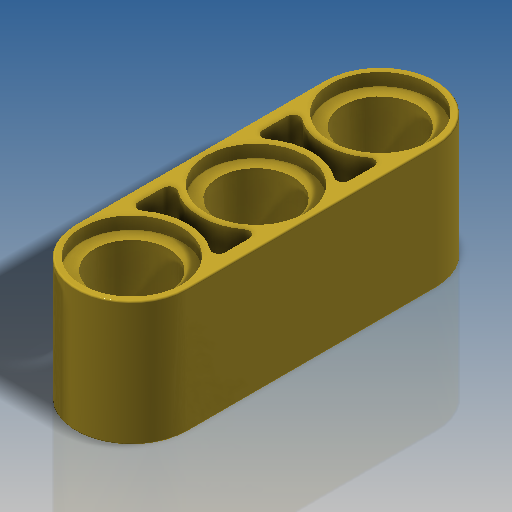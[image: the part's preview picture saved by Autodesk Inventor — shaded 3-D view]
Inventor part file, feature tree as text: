
AUTODESK INVENTOR PART (.ipt)
format: ipt  version: 2018.3 (Build 223284000, 284)  size: 294,400 bytes
history: native  units: mm
features: extrude x3, sketch x2, mirror x1, fillet x1
ambient origin geometry x8: Origin, YZ Plane, XZ Plane, XY Plane, X Axis, Y Axis, Z Axis, Center Point
bodies: Solid1 (feature_tree)
feature tree (7):
  extrude  "Extrusion1"  Depth=6.4mm
  sketch  "Sketch6"  dims[d14=8.0mm d15=0.0mm d32=7.2mm d34=8.0mm d36=0.8mm d41=0.8mm d42=0.0mm d43=3.1mm d44=0.0mm d45=0.1mm d46=0.4mm]
  extrude  "Extrusion7"  Depth=7.2mm
  extrude  "Extrusion8"  Depth=8.0mm
  mirror  "Mirror1"
  fillet  "Fillet1"  Radius=0.8mm
  sketch  "Sketch1"  dims[d8=4.8mm d9=6.4mm]
